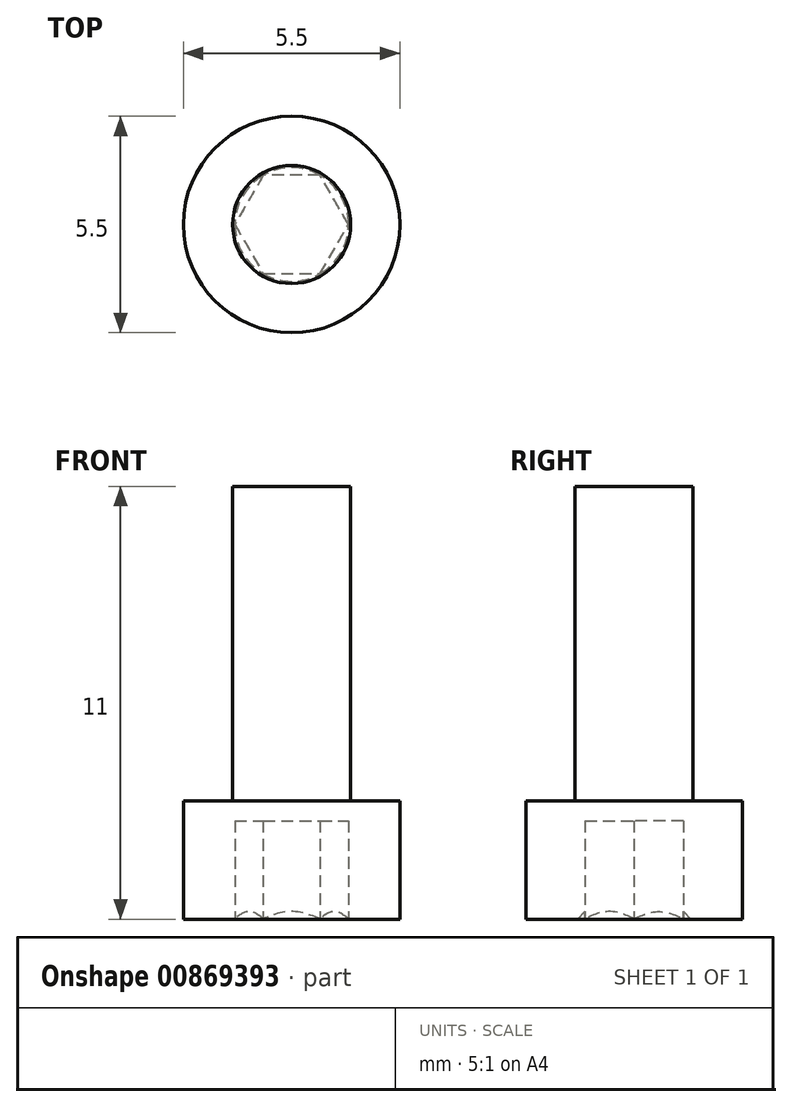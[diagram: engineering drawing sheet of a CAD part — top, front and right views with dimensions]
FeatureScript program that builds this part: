
annotation { "Feature Type Name" : "Feature", "Feature Type Description" : "" }
export const myFeature = defineFeature(function(context is Context, id is Id, definition is map)
    precondition{}
    {
        {
            var Q0;
            Q0=qCreatedBy(makeId("Top.planeOp"),FACE);
            var sketch = newSketch(context, id + "F0", { "sketchPlane" : qUnion([Q0])});
            skCircle(sketch, "E0", {"center": v(0, 0) * mm, "radius": 2.75 * mm});
            skSolve(sketch);
        }
        {
            var Q0;
            Q0 = qSketchRegion(id + "F0", true);
            extrude(context, id + "F1", {"entities" : qUnion([Q0]), "depth" : 3 * mm, "offsetDistance" : 25 * mm});
        }
        {
            var Q0;
            Q0=makeQuery(id+"F1.opExtrude","CAP_FACE",FACE,{"disambiguationData":[OSD([sQuery(id+"F0.wireOp",EDGE,"E0")])],"isStart":false});
            var sketch = newSketch(context, id + "F2", { "sketchPlane" : qUnion([Q0])});
            skCircle(sketch, "E1", {"center": v(0, 0) * mm, "radius": 1.5 * mm});
            skSolve(sketch);
        }
        {
            var Q0;
            Q0=makeQuery(id+"F2.imprint","IMPRINT",FACE,{"disambiguationData":[TD([[makeQuery(id+"F2.imprint","IMPRINT",EDGE,{"derivedFrom":sQuery(id+"F2.wireOp",EDGE,"E1")}),1.0]])]});
            extrude(context, id + "F3", {"entities" : qUnion([Q0]), "operationType" : NewBodyOperationType.ADD, "depth" : 8 * mm, "offsetDistance" : 25 * mm});
        }
        {
            var Q0;
            Q0=makeQuery(id+"F1.opExtrude","CAP_FACE",FACE,{"disambiguationData":[OSD([sQuery(id+"F0.wireOp",EDGE,"E0")])],"isStart":true});
            var sketch = newSketch(context, id + "F4", { "sketchPlane" : qUnion([Q0])});
            skCircle(sketch, "E2", {"center": v(0, 0) * mm, "radius": 1.44 * mm});
            skLineSegment(sketch, "E3", {"start": v(-0.72, 1.25) * mm, "end": v(0.72, 1.25) * mm});
            skLineSegment(sketch, "E4", {"start": v(0.72, 1.25) * mm, "end": v(1.44, 0) * mm});
            skLineSegment(sketch, "E5", {"start": v(1.44, 0) * mm, "end": v(0.72, -1.25) * mm});
            skLineSegment(sketch, "E6", {"start": v(0.72, -1.25) * mm, "end": v(-0.72, -1.25) * mm});
            skLineSegment(sketch, "E7", {"start": v(-0.72, -1.25) * mm, "end": v(-1.44, 0) * mm});
            skLineSegment(sketch, "E8", {"start": v(-1.44, 0) * mm, "end": v(-0.72, 1.25) * mm});
            skSolve(sketch);
        }
        {
            var Q0;
            Q0=makeQuery(id+"F4.imprint","IMPRINT",FACE,{"disambiguationData":[TD([[makeQuery(id+"F4.imprint","IMPRINT",EDGE,{"derivedFrom":sQuery(id+"F4.wireOp",EDGE,"E3")}),-1.0]])]});
            extrude(context, id + "F5", {"entities" : qUnion([Q0]), "operationType" : NewBodyOperationType.REMOVE, "oppositeDirection" : true, "depth" : 2.5 * mm, "offsetDistance" : 25 * mm});
        }
        {
            var Q0;
            {var subQ0=sQuery(id+"F4.wireOp",EDGE,"E8");Q0=makeQuery(id+"F4.imprint","IMPRINT",FACE,{"disambiguationData":[TD([[makeQuery(id+"F4.imprint","IMPRINT",EDGE,{"derivedFrom":subQ0}),1.0]])]});}
            var Q1;
            {var subQ0=sQuery(id+"F4.wireOp",EDGE,"E3");Q1=makeQuery(id+"F4.imprint","IMPRINT",FACE,{"disambiguationData":[TD([[makeQuery(id+"F4.imprint","IMPRINT",EDGE,{"derivedFrom":subQ0}),1.0]])]});}
            var Q2;
            {var subQ0=sQuery(id+"F4.wireOp",EDGE,"E4");Q2=makeQuery(id+"F4.imprint","IMPRINT",FACE,{"disambiguationData":[TD([[makeQuery(id+"F4.imprint","IMPRINT",EDGE,{"derivedFrom":subQ0}),1.0]])]});}
            var Q3;
            {var subQ0=sQuery(id+"F4.wireOp",EDGE,"E5");Q3=makeQuery(id+"F4.imprint","IMPRINT",FACE,{"disambiguationData":[TD([[makeQuery(id+"F4.imprint","IMPRINT",EDGE,{"derivedFrom":subQ0}),1.0]])]});}
            var Q4;
            {var subQ0=sQuery(id+"F4.wireOp",EDGE,"E7");Q4=makeQuery(id+"F4.imprint","IMPRINT",FACE,{"disambiguationData":[TD([[makeQuery(id+"F4.imprint","IMPRINT",EDGE,{"derivedFrom":subQ0}),1.0]])]});}
            var Q5;
            Q5=makeQuery(id+"F4.imprint","IMPRINT",FACE,{"disambiguationData":[TD([[makeQuery(id+"F4.imprint","IMPRINT",EDGE,{"derivedFrom":sQuery(id+"F4.wireOp",EDGE,"E3")}),-1.0]])]});
            var Q6;
            {var subQ0=sQuery(id+"F4.wireOp",EDGE,"E6");Q6=makeQuery(id+"F4.imprint","IMPRINT",FACE,{"disambiguationData":[TD([[makeQuery(id+"F4.imprint","IMPRINT",EDGE,{"derivedFrom":subQ0}),1.0]])]});}
            extrude(context, id + "F6", {"entities" : qUnion([Q0, Q1, Q2, Q3, Q4, Q5, Q6]), "operationType" : NewBodyOperationType.REMOVE, "oppositeDirection" : true, "depth" : 2.5 * mm, "offsetDistance" : 25 * mm, "hasDraft" : true, "draftAngle" : 45 * degree, "draftPullDirection" : true});
        }
    });
